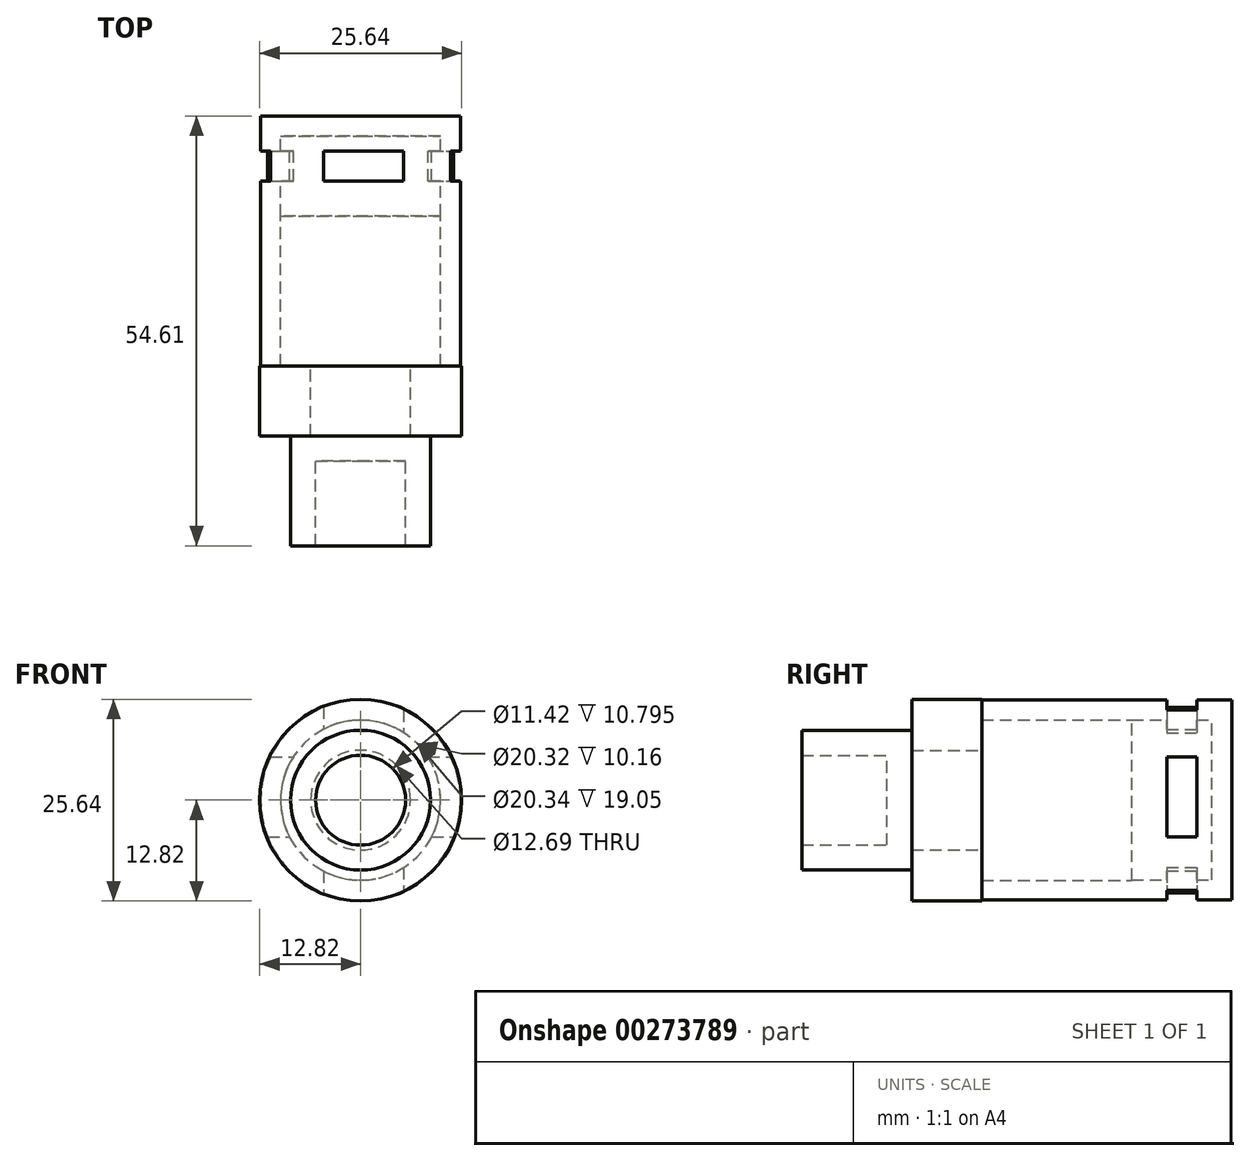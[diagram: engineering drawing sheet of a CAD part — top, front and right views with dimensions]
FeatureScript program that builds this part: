
annotation { "Feature Type Name" : "Feature", "Feature Type Description" : "" }
export const myFeature = defineFeature(function(context is Context, id is Id, definition is map)
    precondition{}
    {
        {
            var Q0;
            Q0=qCreatedBy(makeId("Front.planeOp"),FACE);
            var sketch = newSketch(context, id + "F0", { "sketchPlane" : qUnion([Q0])});
            skCircle(sketch, "E0", {"center": v(0, 0) * mm, "radius": 12.7 * mm});
            skSolve(sketch);
        }
        {
            var Q0;
            Q0=makeQuery(id+"F0.imprint","IMPRINT",FACE,{"disambiguationData":[TD([[makeQuery(id+"F0.imprint","IMPRINT",EDGE,{"derivedFrom":sQuery(id+"F0.wireOp",EDGE,"E0")}),1.0]])]});
            extrude(context, id + "F1", {"entities" : qUnion([Q0]), "depth" : 12.7 * mm});
        }
        {
            var Q0;
            Q0=qCreatedBy(makeId("Right.planeOp"),FACE);
            var sketch = newSketch(context, id + "F2", { "sketchPlane" : qUnion([Q0])});
            skLineSegment(sketch, "E1.bottom", {"start": v(-4.45, 5.5) * mm, "end": v(-8.26, 5.5) * mm});
            skLineSegment(sketch, "E1.top", {"start": v(-4.44, -4.66) * mm, "end": v(-8.25, -4.66) * mm});
            skLineSegment(sketch, "E1.left", {"start": v(-4.45, 5.5) * mm, "end": v(-4.44, -4.66) * mm});
            skLineSegment(sketch, "E1.right", {"start": v(-8.26, 5.5) * mm, "end": v(-8.26, -4.66) * mm});
            skSolve(sketch);
        }
        {
            var Q0;
            Q0=qCreatedBy(makeId("Top.planeOp"),FACE);
            var sketch = newSketch(context, id + "F3", { "sketchPlane" : qUnion([Q0])});
            skLineSegment(sketch, "E2.bottom", {"start": v(-4.68, -4.45) * mm, "end": v(5.48, -4.45) * mm});
            skLineSegment(sketch, "E2.top", {"start": v(-4.68, -8.25) * mm, "end": v(5.48, -8.25) * mm});
            skLineSegment(sketch, "E2.left", {"start": v(-4.68, -4.45) * mm, "end": v(-4.68, -8.25) * mm});
            skLineSegment(sketch, "E2.right", {"start": v(5.48, -4.45) * mm, "end": v(5.48, -8.25) * mm});
            skSolve(sketch);
        }
        {
            var Q0;
            Q0=makeQuery(id+"F1.opExtrude","CAP_FACE",FACE,{"disambiguationData":[OSD([sQuery(id+"F0.wireOp",EDGE,"E0")])],"isStart":false});
            shell(context, id + "F4", {"entities" : qUnion([Q0]), "thickness" : 2.54 * mm});
        }
        {
            var Q0;
            Q0 = qSketchRegion(id + "F2", true);
            extrude(context, id + "F5", {"entities" : qUnion([Q0]), "operationType" : NewBodyOperationType.REMOVE, "endBound" : BoundingType.SYMMETRIC, "oppositeDirection" : true, "depth" : 25.4 * mm});
        }
        {
            var Q0;
            Q0 = qSketchRegion(id + "F3", true);
            extrude(context, id + "F6", {"entities" : qUnion([Q0]), "operationType" : NewBodyOperationType.REMOVE, "endBound" : BoundingType.SYMMETRIC, "depth" : 25.4 * mm});
        }
        {
            var Q0;
            Q0=qCreatedBy(makeId("Front.planeOp"),FACE);
            cPlane(context, id + "F7", {"entities" : qUnion([Q0]), "cplaneType" : CPlaneType.OFFSET, "offset" : 12.7 * mm, "width" : 152.4 * mm, "height" : 152.4 * mm});
        }
        {
            var Q0;
            Q0=qCreatedBy(id+"F7.planeOp",FACE);
            var sketch = newSketch(context, id + "F8", { "sketchPlane" : qUnion([Q0])});
            skCircle(sketch, "E3", {"center": v(0, 0) * mm, "radius": 12.7 * mm});
            skCircle(sketch, "E4", {"center": v(0, 0) * mm, "radius": 10.17 * mm});
            skSolve(sketch);
        }
        {
            var Q0;
            Q0=makeQuery(id+"F8.imprint","IMPRINT",FACE,{"disambiguationData":[TD([[makeQuery(id+"F8.imprint","IMPRINT",EDGE,{"derivedFrom":sQuery(id+"F8.wireOp",EDGE,"E3")}),1.0]])]});
            extrude(context, id + "F9", {"entities" : qUnion([Q0]), "operationType" : NewBodyOperationType.ADD, "depth" : 19.05 * mm});
        }
        {
            var Q0;
            Q0=qCreatedBy(id+"F7.planeOp",FACE);
            cPlane(context, id + "F10", {"entities" : qUnion([Q0]), "cplaneType" : CPlaneType.OFFSET, "offset" : 19.05 * mm, "width" : 152.4 * mm, "height" : 152.4 * mm});
        }
        {
            var Q0;
            Q0=qCreatedBy(id+"F10.planeOp",FACE);
            var sketch = newSketch(context, id + "F11", { "sketchPlane" : qUnion([Q0])});
            skCircle(sketch, "E5", {"center": v(0, 0) * mm, "radius": 12.82 * mm});
            skSolve(sketch);
        }
        {
            var Q0;
            Q0=makeQuery(id+"F11.imprint","IMPRINT",FACE,{"disambiguationData":[TD([[makeQuery(id+"F11.imprint","IMPRINT",EDGE,{"derivedFrom":sQuery(id+"F11.wireOp",EDGE,"E5")}),1.0]])]});
            extrude(context, id + "F12", {"entities" : qUnion([Q0]), "operationType" : NewBodyOperationType.ADD, "depth" : 8.9 * mm});
        }
        {
            var Q0;
            Q0=qCreatedBy(id+"F10.planeOp",FACE);
            var sketch = newSketch(context, id + "F13", { "sketchPlane" : qUnion([Q0])});
            skCircle(sketch, "E6", {"center": v(0, 0) * mm, "radius": 6.35 * mm});
            skSolve(sketch);
        }
        {
            var Q0;
            Q0 = qSketchRegion(id + "F13", true);
            extrude(context, id + "F14", {"entities" : qUnion([Q0]), "operationType" : NewBodyOperationType.REMOVE, "depth" : 10.4 * mm});
        }
        {
            var Q0;
            Q0=qCreatedBy(id+"F10.planeOp",FACE);
            cPlane(context, id + "F15", {"entities" : qUnion([Q0]), "cplaneType" : CPlaneType.OFFSET, "offset" : 8.9 * mm, "width" : 152.4 * mm, "height" : 152.4 * mm});
        }
        {
            var Q0;
            Q0=qCreatedBy(id+"F15.planeOp",FACE);
            var sketch = newSketch(context, id + "F16", { "sketchPlane" : qUnion([Q0])});
            skCircle(sketch, "E7", {"center": v(0, 0) * mm, "radius": 8.89 * mm});
            skSolve(sketch);
        }
        {
            var Q0;
            Q0 = qSketchRegion(id + "F16", true);
            extrude(context, id + "F17", {"entities" : qUnion([Q0]), "depth" : 13.97 * mm});
        }
        {
            var Q0;
            Q0=makeQuery(id+"F17.opExtrude","CAP_FACE",FACE,{"disambiguationData":[OSD([sQuery(id+"F16.wireOp",EDGE,"E7")])],"isStart":false});
            shell(context, id + "F18", {"entities" : qUnion([Q0]), "thickness" : 3.17 * mm});
        }
    });
